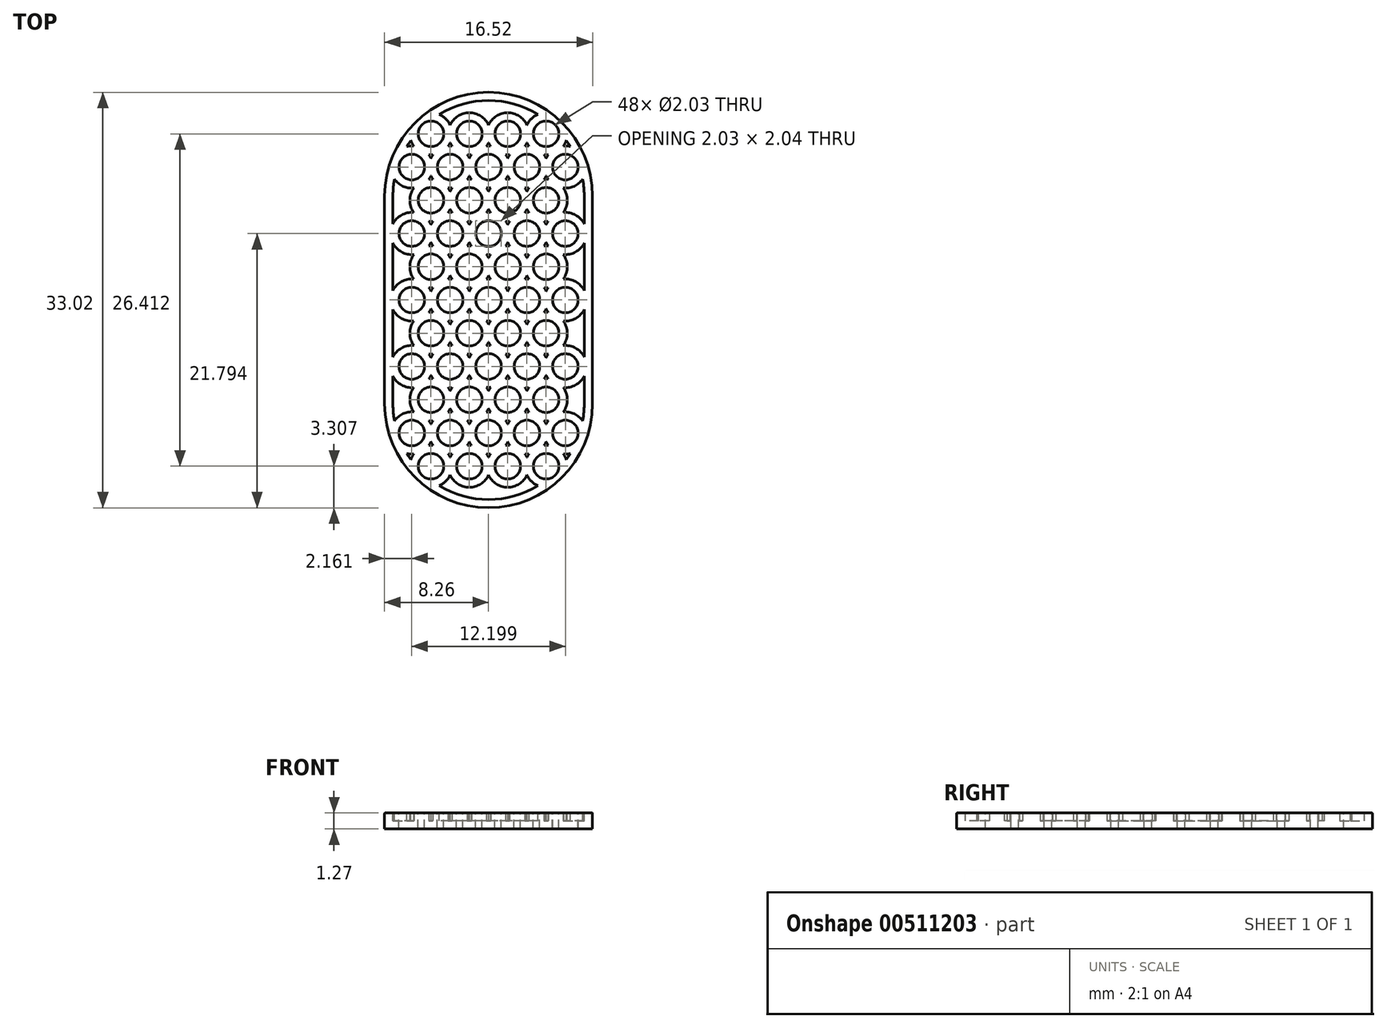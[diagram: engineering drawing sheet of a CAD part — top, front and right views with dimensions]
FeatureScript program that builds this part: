
annotation { "Feature Type Name" : "Feature", "Feature Type Description" : "" }
export const myFeature = defineFeature(function(context is Context, id is Id, definition is map)
    precondition{}
    {
        {
            var Q0;
            Q0=qCreatedBy(makeId("Top.planeOp"),FACE);
            var sketch = newSketch(context, id + "F0", { "sketchPlane" : qUnion([Q0])});
            skCircle(sketch, "E0", {"center": v(0, -13.21) * mm, "radius": 8.26 * mm});
            skCircle(sketch, "E1", {"center": v(0, -29.72) * mm, "radius": 8.26 * mm});
            skLineSegment(sketch, "E2", {"start": v(8.26, -13.21) * mm, "end": v(8.26, -29.72) * mm});
            skLineSegment(sketch, "E3", {"start": v(-8.26, -13.21) * mm, "end": v(-8.26, -29.72) * mm});
            skSolve(sketch);
        }
        {
            var Q0;
            Q0=qSketchRegion(id+"F0",true);
            extrude(context, id + "F1", {"entities" : qUnion([Q0]), "depth" : 1.27 * mm});
        }
        {
            var Q0;
            Q0=makeQuery(id+"F1.opExtrude","CAP_FACE",FACE,{"disambiguationData":[OSD([sQuery(id+"F0.wireOp",EDGE,"E0"),sQuery(id+"F0.wireOp",EDGE,"E1"),sQuery(id+"F0.wireOp",EDGE,"E2"),sQuery(id+"F0.wireOp",EDGE,"E3")])],"isStart":false});
            fillet(context, id + "F2", {"entities" : qUnion([Q0]), "radius" : 0.05 * mm, "tangentPropagation" : true, "allowEdgeOverflow" : false});
        }
        {
            var Q0;
            Q0=makeQuery(id+"F1.opExtrude","CAP_FACE",FACE,{"disambiguationData":[OSD([sQuery(id+"F0.wireOp",EDGE,"E0"),sQuery(id+"F0.wireOp",EDGE,"E1"),sQuery(id+"F0.wireOp",EDGE,"E2"),sQuery(id+"F0.wireOp",EDGE,"E3")])],"isStart":false});
            var sketch = newSketch(context, id + "F3", { "sketchPlane" : qUnion([Q0])});
            skCircle(sketch, "E4", {"center": v(0, -21.47) * mm, "radius": 1.02 * mm});
            skPoint(sketch, "E4.centerSnap0", {"position": v(-8.2, -21.47) * mm});
            skCircle(sketch, "E5", {"center": v(3.05, -21.47) * mm, "radius": 1.02 * mm});
            skLineSegment(sketch, "E6", {"start": v(0, -21.47) * mm, "end": v(1.52, -18.83) * mm, "construction": true});
            skLineSegment(sketch, "E7", {"start": v(1.52, -18.83) * mm, "end": v(3.05, -21.47) * mm, "construction": true});
            skLineSegment(sketch, "E8", {"start": v(0, -21.47) * mm, "end": v(3.05, -21.47) * mm, "construction": true});
            skCircle(sketch, "E9", {"center": v(1.52, -18.83) * mm, "radius": 1.02 * mm});
            skLineSegment(sketch, "E10", {"start": v(1.52, -18.83) * mm, "end": v(4.57, -18.83) * mm, "construction": true});
            skLineSegment(sketch, "E11", {"start": v(4.57, -18.83) * mm, "end": v(3.05, -21.47) * mm, "construction": true});
            skCircle(sketch, "E12", {"center": v(4.57, -18.83) * mm, "radius": 1.02 * mm});
            skLineSegment(sketch, "E13", {"start": v(1.52, -18.83) * mm, "end": v(0, -16.19) * mm, "construction": true});
            skLineSegment(sketch, "E14", {"start": v(1.52, -18.83) * mm, "end": v(-1.52, -18.83) * mm, "construction": true});
            skLineSegment(sketch, "E15", {"start": v(-1.52, -18.83) * mm, "end": v(0, -16.19) * mm, "construction": true});
            skCircle(sketch, "E16", {"center": v(0, -16.19) * mm, "radius": 1.02 * mm});
            skCircle(sketch, "E17.0.1.0", {"center": v(0, -16.18) * mm, "radius": 1.02 * mm});
            skCircle(sketch, "E17.0.1.1", {"center": v(3.05, -16.18) * mm, "radius": 1.02 * mm});
            skCircle(sketch, "E17.0.1.2", {"center": v(1.52, -13.54) * mm, "radius": 1.02 * mm});
            skCircle(sketch, "E17.0.1.3", {"center": v(4.57, -13.54) * mm, "radius": 1.02 * mm});
            skCircle(sketch, "E17.0.2.0", {"center": v(0, -10.9) * mm, "radius": 1.02 * mm});
            skCircle(sketch, "E17.0.2.1", {"center": v(3.05, -10.9) * mm, "radius": 1.02 * mm});
            skCircle(sketch, "E17.0.2.2", {"center": v(1.52, -8.26) * mm, "radius": 1.02 * mm});
            skCircle(sketch, "E17.0.2.3", {"center": v(4.57, -8.26) * mm, "radius": 1.02 * mm});
            skLineSegment(sketch, "E17.direction1", {"start": v(0, -21.47) * mm, "end": v(25.4, -21.47) * mm, "construction": true});
            skLineSegment(sketch, "E17.direction2", {"start": v(0, -21.47) * mm, "end": v(0, -16.18) * mm, "construction": true});
            skLineSegment(sketch, "E18", {"start": v(4.57, -13.54) * mm, "end": v(3.05, -10.9) * mm, "construction": true});
            skLineSegment(sketch, "E19", {"start": v(3.05, -10.9) * mm, "end": v(6.1, -10.9) * mm, "construction": true});
            skLineSegment(sketch, "E20", {"start": v(6.1, -10.9) * mm, "end": v(4.57, -13.54) * mm, "construction": true});
            skCircle(sketch, "E21", {"center": v(6.1, -10.9) * mm, "radius": 1.02 * mm});
            skLineSegment(sketch, "E22", {"start": v(4.57, -13.54) * mm, "end": v(6.1, -16.18) * mm, "construction": true});
            skLineSegment(sketch, "E23", {"start": v(6.1, -16.18) * mm, "end": v(3.05, -16.18) * mm, "construction": true});
            skLineSegment(sketch, "E24", {"start": v(3.05, -16.18) * mm, "end": v(4.57, -13.54) * mm, "construction": true});
            skCircle(sketch, "E25", {"center": v(6.1, -16.18) * mm, "radius": 1.02 * mm});
            skLineSegment(sketch, "E26", {"start": v(3.05, -21.47) * mm, "end": v(6.1, -21.47) * mm, "construction": true});
            skLineSegment(sketch, "E27", {"start": v(6.1, -21.47) * mm, "end": v(4.57, -18.83) * mm, "construction": true});
            skCircle(sketch, "E28", {"center": v(6.1, -21.47) * mm, "radius": 1.02 * mm});
            skLineSegment(sketch, "E29", {"start": v(-8.2, -21.47) * mm, "end": v(10.53, -21.47) * mm, "construction": true});
            skLineSegment(sketch, "E30", {"start": v(0, -5) * mm, "end": v(0, -37.93) * mm, "construction": true});
            skCircle(sketch, "E31.MirrorC", {"center": v(-1.52, -8.26) * mm, "radius": 1.02 * mm});
            skCircle(sketch, "E32.MirrorC", {"center": v(-4.57, -8.26) * mm, "radius": 1.02 * mm});
            skLineSegment(sketch, "E33.MirrorCS", {"start": v(-3.05, -10.9) * mm, "end": v(-6.1, -10.9) * mm, "construction": true});
            skCircle(sketch, "E34.MirrorC", {"center": v(-6.1, -10.9) * mm, "radius": 1.02 * mm});
            skCircle(sketch, "E35.MirrorC", {"center": v(-3.05, -10.9) * mm, "radius": 1.02 * mm});
            skCircle(sketch, "E36.MirrorC", {"center": v(-1.52, -13.54) * mm, "radius": 1.02 * mm});
            skCircle(sketch, "E37.MirrorC", {"center": v(-4.57, -13.54) * mm, "radius": 1.02 * mm});
            skCircle(sketch, "E38.MirrorC", {"center": v(-6.1, -16.18) * mm, "radius": 1.02 * mm});
            skCircle(sketch, "E39.MirrorC", {"center": v(-3.05, -16.18) * mm, "radius": 1.02 * mm});
            skCircle(sketch, "E40.MirrorC", {"center": v(-1.52, -18.83) * mm, "radius": 1.02 * mm});
            skCircle(sketch, "E41.MirrorC", {"center": v(-4.57, -18.83) * mm, "radius": 1.02 * mm});
            skCircle(sketch, "E42.MirrorC", {"center": v(-3.05, -21.47) * mm, "radius": 1.02 * mm});
            skCircle(sketch, "E43.MirrorC", {"center": v(-6.1, -21.47) * mm, "radius": 1.02 * mm});
            skCircle(sketch, "E44.MirrorC", {"center": v(4.57, -24.1) * mm, "radius": 1.02 * mm});
            skCircle(sketch, "E45.MirrorC", {"center": v(1.52, -24.1) * mm, "radius": 1.02 * mm});
            skCircle(sketch, "E46.MirrorC", {"center": v(-1.52, -24.1) * mm, "radius": 1.02 * mm});
            skCircle(sketch, "E47.MirrorC", {"center": v(-4.57, -24.1) * mm, "radius": 1.02 * mm});
            skCircle(sketch, "E48.MirrorC", {"center": v(-6.1, -26.75) * mm, "radius": 1.02 * mm});
            skCircle(sketch, "E49.MirrorC", {"center": v(-3.05, -26.75) * mm, "radius": 1.02 * mm});
            skCircle(sketch, "E50.MirrorC", {"center": v(0, -26.75) * mm, "radius": 1.02 * mm});
            skCircle(sketch, "E51.MirrorC", {"center": v(3.05, -26.75) * mm, "radius": 1.02 * mm});
            skCircle(sketch, "E52.MirrorC", {"center": v(6.1, -26.75) * mm, "radius": 1.02 * mm});
            skCircle(sketch, "E53.MirrorC", {"center": v(4.57, -29.39) * mm, "radius": 1.02 * mm});
            skCircle(sketch, "E54.MirrorC", {"center": v(1.52, -29.39) * mm, "radius": 1.02 * mm});
            skCircle(sketch, "E55.MirrorC", {"center": v(-1.52, -29.39) * mm, "radius": 1.02 * mm});
            skCircle(sketch, "E56.MirrorC", {"center": v(-4.57, -29.39) * mm, "radius": 1.02 * mm});
            skCircle(sketch, "E57.MirrorC", {"center": v(-6.1, -32.03) * mm, "radius": 1.02 * mm});
            skCircle(sketch, "E58.MirrorC", {"center": v(-3.05, -32.03) * mm, "radius": 1.02 * mm});
            skCircle(sketch, "E59.MirrorC", {"center": v(0, -32.03) * mm, "radius": 1.02 * mm});
            skCircle(sketch, "E60.MirrorC", {"center": v(3.05, -32.03) * mm, "radius": 1.02 * mm});
            skCircle(sketch, "E61.MirrorC", {"center": v(6.1, -32.03) * mm, "radius": 1.02 * mm});
            skCircle(sketch, "E62.MirrorC", {"center": v(4.57, -34.67) * mm, "radius": 1.02 * mm});
            skCircle(sketch, "E63.MirrorC", {"center": v(1.52, -34.67) * mm, "radius": 1.02 * mm});
            skCircle(sketch, "E64.MirrorC", {"center": v(-1.52, -34.67) * mm, "radius": 1.02 * mm});
            skCircle(sketch, "E65.MirrorC", {"center": v(-4.57, -34.67) * mm, "radius": 1.02 * mm});
            skSolve(sketch);
        }
        {
            var Q0;
            Q0=qSketchRegion(id+"F3",true);
            extrude(context, id + "F4", {"entities" : qUnion([Q0]), "operationType" : NewBodyOperationType.REMOVE, "endBound" : BoundingType.THROUGH_ALL, "oppositeDirection" : true, "depth" : 25.4 * mm});
        }
        {
            var Q0;
            Q0=makeQuery(id+"F1.opExtrude","CAP_FACE",FACE,{"disambiguationData":[OSD([sQuery(id+"F0.wireOp",EDGE,"E0"),sQuery(id+"F0.wireOp",EDGE,"E1"),sQuery(id+"F0.wireOp",EDGE,"E2"),sQuery(id+"F0.wireOp",EDGE,"E3")])],"isStart":false});
            shell(context, id + "F5", {"entities" : qUnion([Q0]), "thickness" : 0.66 * mm});
        }
    });
